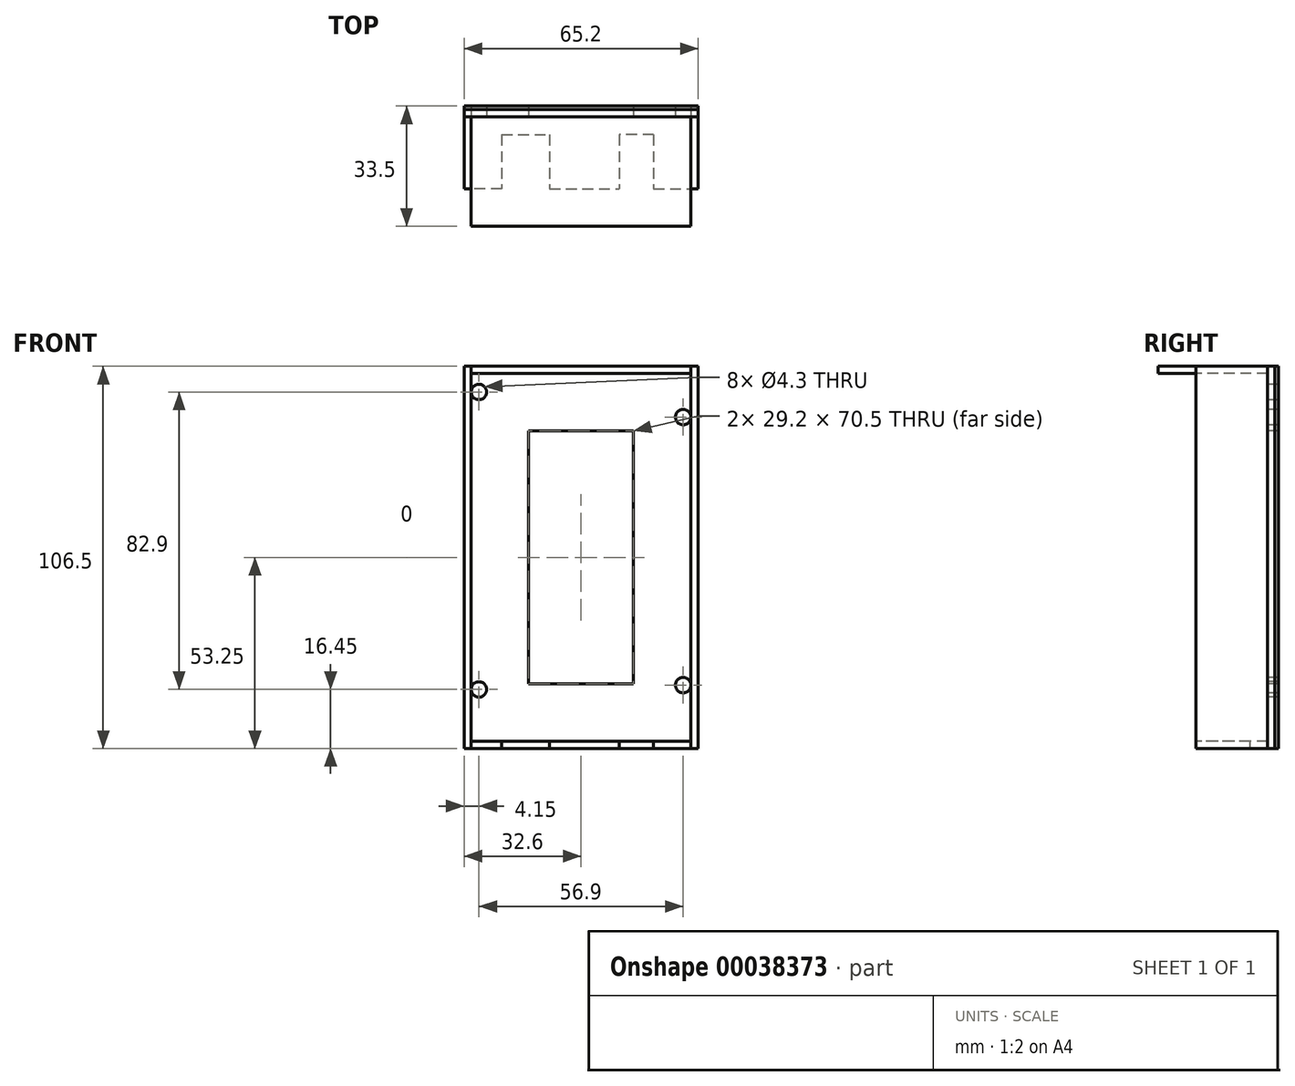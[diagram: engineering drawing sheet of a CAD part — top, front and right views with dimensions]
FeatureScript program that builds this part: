
annotation { "Feature Type Name" : "Feature", "Feature Type Description" : "" }
export const myFeature = defineFeature(function(context is Context, id is Id, definition is map)
    precondition{}
    {
        {
            var Q0;
            Q0=qCreatedBy(makeId("Front.planeOp"),FACE);
            var sketch = newSketch(context, id + "F0", { "sketchPlane" : qUnion([Q0])});
            skLineSegment(sketch, "E0.bottom", {"start": v(0, 0) * mm, "end": v(65.2, 0) * mm});
            skLineSegment(sketch, "E0.top", {"start": v(0, -106.5) * mm, "end": v(65.2, -106.5) * mm});
            skLineSegment(sketch, "E0.left", {"start": v(0, 0) * mm, "end": v(0, -106.5) * mm});
            skLineSegment(sketch, "E0.right", {"start": v(65.2, 0) * mm, "end": v(65.2, -106.5) * mm});
            skLineSegment(sketch, "E1", {"start": v(0, 0) * mm, "end": v(18, 0) * mm, "construction": true});
            skLineSegment(sketch, "E2", {"start": v(18, 0) * mm, "end": v(18, -18) * mm, "construction": true});
            skLineSegment(sketch, "E3", {"start": v(18, -18) * mm, "end": v(0, -18) * mm, "construction": true});
            skLineSegment(sketch, "E4", {"start": v(0, -18) * mm, "end": v(0, 0) * mm, "construction": true});
            skLineSegment(sketch, "E5.bottom", {"start": v(65.2, -106.5) * mm, "end": v(47.2, -106.5) * mm, "construction": true});
            skLineSegment(sketch, "E5.top", {"start": v(65.2, -88.5) * mm, "end": v(47.2, -88.5) * mm, "construction": true});
            skLineSegment(sketch, "E5.left", {"start": v(65.2, -106.5) * mm, "end": v(65.2, -88.5) * mm, "construction": true});
            skLineSegment(sketch, "E5.right", {"start": v(47.2, -106.5) * mm, "end": v(47.2, -88.5) * mm, "construction": true});
            skLineSegment(sketch, "E6", {"start": v(18, -18) * mm, "end": v(18, -88.5) * mm});
            skLineSegment(sketch, "E7", {"start": v(18, -88.5) * mm, "end": v(47.2, -88.5) * mm});
            skLineSegment(sketch, "E8", {"start": v(47.2, -18) * mm, "end": v(47.2, -88.5) * mm});
            skLineSegment(sketch, "E9", {"start": v(47.2, -18) * mm, "end": v(18, -18) * mm});
            skLineSegment(sketch, "E10", {"start": v(0, -2) * mm, "end": v(2, -2) * mm, "construction": true});
            skLineSegment(sketch, "E11", {"start": v(2, -2) * mm, "end": v(2, 0) * mm, "construction": true});
            skLineSegment(sketch, "E12", {"start": v(65.2, -104.5) * mm, "end": v(63.2, -104.5) * mm, "construction": true});
            skLineSegment(sketch, "E13", {"start": v(63.2, -104.5) * mm, "end": v(63.2, -106.5) * mm, "construction": true});
            skLineSegment(sketch, "E14.bottom", {"start": v(2, -2) * mm, "end": v(63.2, -2) * mm, "construction": true});
            skLineSegment(sketch, "E14.top", {"start": v(2, -104.5) * mm, "end": v(63.2, -104.5) * mm, "construction": true});
            skLineSegment(sketch, "E14.left", {"start": v(2, -2) * mm, "end": v(2, -104.5) * mm, "construction": true});
            skLineSegment(sketch, "E14.right", {"start": v(63.2, -2) * mm, "end": v(63.2, -104.5) * mm, "construction": true});
            skLineSegment(sketch, "E15", {"start": v(2, -2) * mm, "end": v(4.15, -2) * mm, "construction": true});
            skLineSegment(sketch, "E16", {"start": v(4.15, -2) * mm, "end": v(4.15, -7.15) * mm, "construction": true});
            skCircle(sketch, "E17", {"center": v(4.15, -7.15) * mm, "radius": 2.15 * mm});
            skLineSegment(sketch, "E18", {"start": v(63.2, -2) * mm, "end": v(61.05, -2) * mm, "construction": true});
            skLineSegment(sketch, "E19", {"start": v(61.05, -2) * mm, "end": v(61.05, -14.15) * mm, "construction": true});
            skCircle(sketch, "E20", {"center": v(61.05, -14.15) * mm, "radius": 2.15 * mm});
            skLineSegment(sketch, "E21", {"start": v(2, -104.5) * mm, "end": v(4.15, -104.5) * mm, "construction": true});
            skLineSegment(sketch, "E22", {"start": v(4.15, -104.5) * mm, "end": v(4.15, -90.05) * mm, "construction": true});
            skCircle(sketch, "E23", {"center": v(4.15, -90.05) * mm, "radius": 2.15 * mm});
            skLineSegment(sketch, "E24", {"start": v(63.2, -104.5) * mm, "end": v(61.05, -104.5) * mm});
            skLineSegment(sketch, "E25", {"start": v(61.05, -104.5) * mm, "end": v(61.05, -88.85) * mm});
            skCircle(sketch, "E26", {"center": v(61.05, -88.85) * mm, "radius": 2.15 * mm});
            skSolve(sketch);
        }
        {
            var Q0;
            Q0=qSketchRegion(id+"F0",true);
            extrude(context, id + "F1", {"entities" : qUnion([Q0]), "oppositeDirection" : true, "depth" : 3 * mm});
        }
        {
            var Q0;
            Q0=makeQuery(id+"F1.opExtrude","SWEPT_FACE",FACE,{"disambiguationData":[OSD([sQuery(id+"F0.wireOp",EDGE,"E0.right")])]});
            var sketch = newSketch(context, id + "F2", { "sketchPlane" : qUnion([Q0])});
            skLineSegment(sketch, "E27.bottom", {"start": v(0, -106.5) * mm, "end": v(-20, -106.5) * mm});
            skLineSegment(sketch, "E27.top", {"start": v(0, 0) * mm, "end": v(-20, 0) * mm});
            skLineSegment(sketch, "E27.left", {"start": v(0, -106.5) * mm, "end": v(0, 0) * mm});
            skLineSegment(sketch, "E27.right", {"start": v(-20, -106.5) * mm, "end": v(-20, 0) * mm});
            skSolve(sketch);
        }
        {
            var Q0;
            Q0=qSketchRegion(id+"F2",true);
            extrude(context, id + "F3", {"entities" : qUnion([Q0]), "oppositeDirection" : true, "depth" : 2 * mm});
        }
        {
            var Q0;
            Q0=makeQuery(id+"F1.opExtrude","SWEPT_FACE",FACE,{"disambiguationData":[OSD([sQuery(id+"F0.wireOp",EDGE,"E0.left")])]});
            var sketch = newSketch(context, id + "F4", { "sketchPlane" : qUnion([Q0])});
            skLineSegment(sketch, "E28.bottom", {"start": v(0, 0) * mm, "end": v(20, 0) * mm});
            skLineSegment(sketch, "E28.top", {"start": v(0, -106.5) * mm, "end": v(20, -106.5) * mm});
            skLineSegment(sketch, "E28.left", {"start": v(0, 0) * mm, "end": v(0, -106.5) * mm});
            skLineSegment(sketch, "E28.right", {"start": v(20, 0) * mm, "end": v(20, -106.5) * mm});
            skSolve(sketch);
        }
        {
            var Q0;
            Q0=qSketchRegion(id+"F4",true);
            extrude(context, id + "F5", {"entities" : qUnion([Q0]), "oppositeDirection" : true, "depth" : 2 * mm});
        }
        {
            var Q0;
            Q0=makeQuery(id+"F1.opExtrude","SWEPT_FACE",FACE,{"disambiguationData":[OSD([sQuery(id+"F0.wireOp",EDGE,"E0.bottom")])]});
            var sketch = newSketch(context, id + "F6", { "sketchPlane" : qUnion([Q0])});
            skLineSegment(sketch, "E29", {"start": v(65.2, 0) * mm, "end": v(63.2, 0) * mm, "construction": true});
            skLineSegment(sketch, "E30.bottom", {"start": v(63.2, 0) * mm, "end": v(2, 0) * mm});
            skLineSegment(sketch, "E30.top", {"start": v(63.2, -30.5) * mm, "end": v(2, -30.5) * mm});
            skLineSegment(sketch, "E30.left", {"start": v(63.2, 0) * mm, "end": v(63.2, -30.5) * mm});
            skLineSegment(sketch, "E30.right", {"start": v(2, 0) * mm, "end": v(2, -30.5) * mm});
            skSolve(sketch);
        }
        {
            var Q0;
            Q0=qSketchRegion(id+"F6",true);
            extrude(context, id + "F7", {"entities" : qUnion([Q0]), "oppositeDirection" : true, "depth" : 2 * mm});
        }
        {
            var Q0;
            Q0=makeQuery(id+"F1.opExtrude","SWEPT_FACE",FACE,{"disambiguationData":[OSD([sQuery(id+"F0.wireOp",EDGE,"E0.top")])]});
            var sketch = newSketch(context, id + "F8", { "sketchPlane" : qUnion([Q0])});
            skLineSegment(sketch, "E31", {"start": v(0, 0) * mm, "end": v(2, 0) * mm, "construction": true});
            skLineSegment(sketch, "E32", {"start": v(2, 0) * mm, "end": v(2, 5) * mm, "construction": true});
            skLineSegment(sketch, "E33", {"start": v(2, 5) * mm, "end": v(10.5, 5) * mm, "construction": true});
            skLineSegment(sketch, "E34", {"start": v(10.5, 5) * mm, "end": v(23.8, 5) * mm, "construction": true});
            skLineSegment(sketch, "E35", {"start": v(23.8, 5) * mm, "end": v(43.3, 5) * mm, "construction": true});
            skLineSegment(sketch, "E36", {"start": v(43.3, 5) * mm, "end": v(52.8, 5) * mm, "construction": true});
            skLineSegment(sketch, "E37.bottom", {"start": v(2, 0) * mm, "end": v(63.2, 0) * mm});
            skLineSegment(sketch, "E37.left", {"start": v(2, 0) * mm, "end": v(2, 20) * mm});
            skLineSegment(sketch, "E37.right", {"start": v(63.2, 0) * mm, "end": v(63.2, 20) * mm});
            skLineSegment(sketch, "E38", {"start": v(10.5, 5) * mm, "end": v(23.8, 5) * mm});
            skLineSegment(sketch, "E39", {"start": v(23.8, 5) * mm, "end": v(23.8, 20) * mm});
            skLineSegment(sketch, "E40", {"start": v(10.5, 5) * mm, "end": v(10.5, 20) * mm});
            skLineSegment(sketch, "E41", {"start": v(52.8, 5) * mm, "end": v(43.3, 5) * mm});
            skLineSegment(sketch, "E42", {"start": v(43.3, 5) * mm, "end": v(43.3, 20) * mm});
            skLineSegment(sketch, "E43", {"start": v(52.8, 5) * mm, "end": v(52.8, 20) * mm});
            skLineSegment(sketch, "E44", {"start": v(10.5, 20) * mm, "end": v(2, 20) * mm});
            skLineSegment(sketch, "E45", {"start": v(23.8, 20) * mm, "end": v(43.3, 20) * mm});
            skLineSegment(sketch, "E46", {"start": v(52.8, 20) * mm, "end": v(63.2, 20) * mm});
            skSolve(sketch);
        }
        {
            var Q0;
            Q0=qSketchRegion(id+"F8",true);
            extrude(context, id + "F9", {"entities" : qUnion([Q0]), "oppositeDirection" : true, "depth" : 2 * mm});
        }
        {
            var Q0;
            Q0=qSketchRegion(id+"F0",true);
            extrude(context, id + "F10", {"entities" : qUnion([Q0]), "oppositeDirection" : true, "depth" : 2 * mm});
        }
    });
